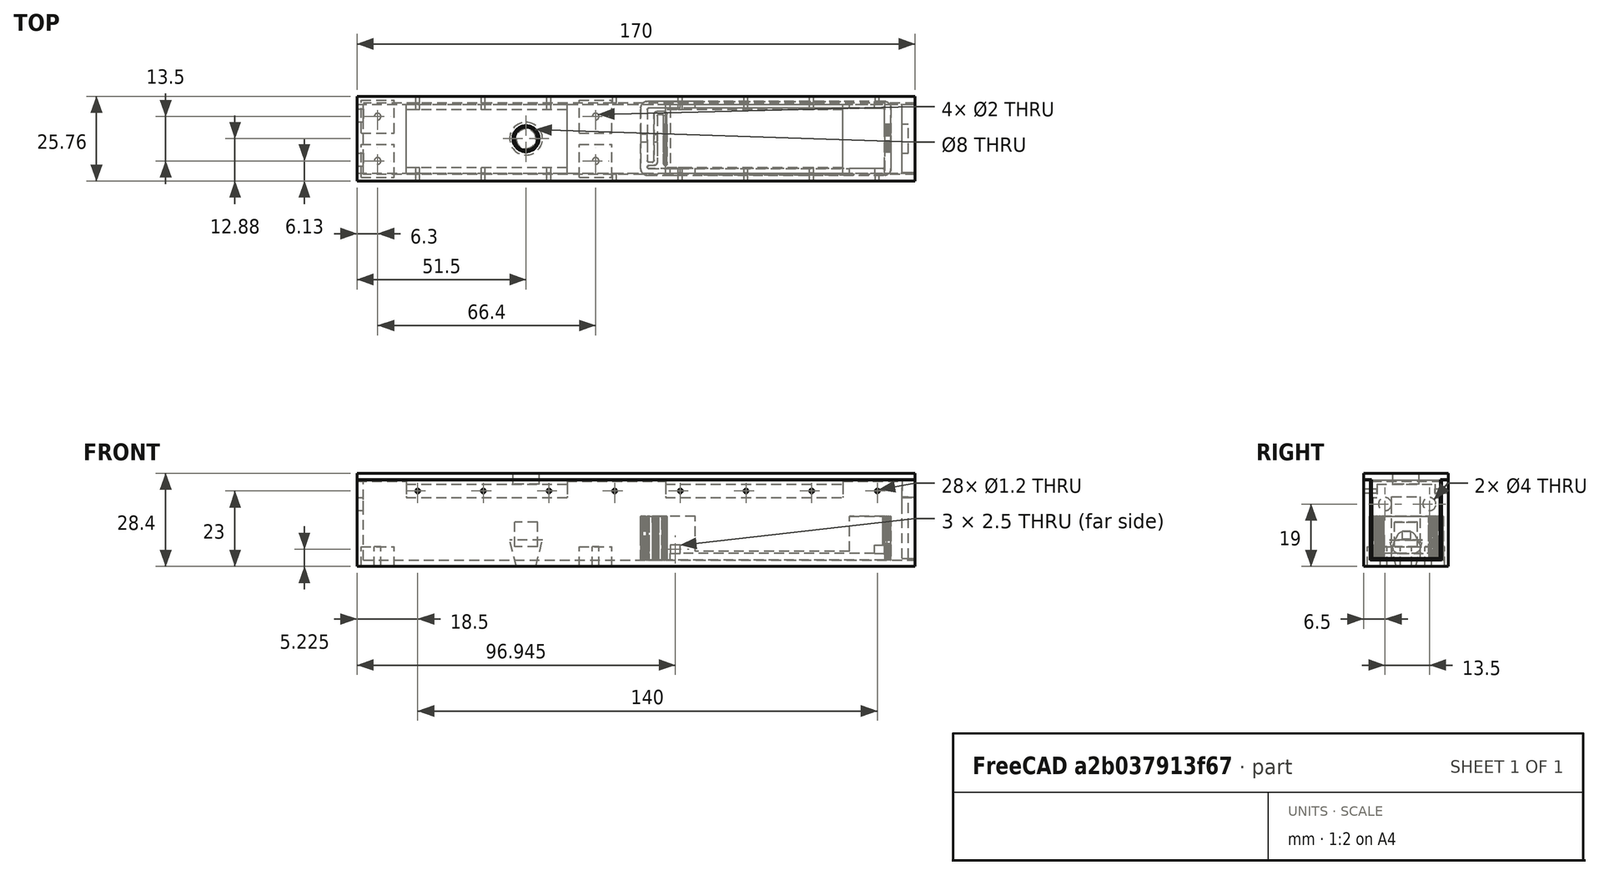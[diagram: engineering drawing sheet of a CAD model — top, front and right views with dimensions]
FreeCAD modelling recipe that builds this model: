
FCSTD DOCUMENT  (FreeCAD 0.19R)
Label: hv-1_box
License: All rights reserved
LicenseURL: http://en.wikipedia.org/wiki/All_rights_reserved
objects: Part::Box×14, Part::Cylinder×5, Part::Cut×5, Part::FeaturePython×4, Part::Feature×4, Part::MultiFuse×3, App::Part×3, Part::Compound×2, Spreadsheet::Sheet×1, Part::Cone×1
note: 38 computed .brp shape members not serialized (recipe doc carries the construction recipe); baked Part::Feature solids carry a one-line shape summary decoded from their .brp

FEATURE [Part::Box] Box  label="Cube"
  AttacherType = Attacher::AttachEngine3D
  Height = 26.3
  Length = 170
  Width = 25.76
  expr: Length = <<p>>.box_sz_x
  expr: Width = <<p>>.box_sz_y
  expr: Height = <<p>>.box_sz_z
FEATURE [Spreadsheet::Sheet] Spreadsheet  label="p"
  cells = A1=pcb_sz_x; B1(pcb_sz_x)=71; A2=pcb_sz_y; B2(pcb_sz_y)=17.76; A3=pcb_sz_z; B3(pcb_sz_z)=1.3; A4=hole_dist_x; B4(hole_dist_x)=66.40000000000001; A5=hole_dist_y; B5(hole_dist_y)=13.5; A6=pcb_under; B6(pcb_under)=4; A7=pcb_above; B7(pcb_above)=11; A8=wall; B8(wall)=2; A9=hole_d; B9(hole_d)=2; A10=box_sz_y; B10(box_sz_y)==pcb_sz_y + 2 * wall + 4; A11=box_sz_x; B11(box_sz_x)==pcb_sz_x + 2 * wall + 95; A12=box_sz_z; B12(box_sz_z)==pcb_under + pcb_sz_z + pcb_above + wall + 8
FEATURE [Part::Cylinder] Cylinder
  Angle = 360
  AttacherType = Attacher::AttachEngine3D
  Height = 14
  Radius = 1
  expr: Radius = <<p>>.hole_d / 2
  expr: Height = <<p>>.pcb_under + 10
FEATURE [Part::Box] Box001  label="Cube001"
  AttacherType = Attacher::AttachEngine3D
  Height = 26.3
  Length = 170
  Placement = pos=(2,2,2) rot=(0,0,1;0rad)
  Width = 21.76
  expr: Length = <<p>>.box_sz_x
  expr: Width = <<p>>.box_sz_y - 2 * <<p>>.wall
  expr: Height = <<p>>.box_sz_z
  expr: .Placement.Base.z = <<p>>.wall
  expr: .Placement.Base.x = <<p>>.wall
  expr: .Placement.Base.y = <<p>>.wall
FEATURE [Part::Cylinder] Cylinder002
  Angle = 360
  AttacherType = Attacher::AttachEngine3D
  Height = 100
  Placement = pos=(18.5,-32.5,23) rot=(-1,0,0;1.5708rad)
  Radius = 0.6
FEATURE [Part::FeaturePython] Array002  # Draft array (typed FeaturePython)
  Angle = 360
  ArrayType = 0
  Axis = (0,0,1)
  Base = -> Cylinder002
  Center = (0,0,0)
  Fuse = false
  IntervalAxis = (0,0,0)
  IntervalX = (20,0,0)
  IntervalY = (0,1,0)
  IntervalZ = (0,0,1)
  NumberPolar = 1
  NumberX = 8
  NumberY = 1
  NumberZ = 1
FEATURE [Part::Box] Box003  label="Cube003"
  AttacherType = Attacher::AttachEngine3D
  Height = 6
  Length = 10
  Placement = pos=(-5,-5,0) rot=(0,0,1;0rad)
  Width = 10
  expr: Height = <<p>>.pcb_under + <<p>>.wall
FEATURE [Part::Cut] Cut
  Base = -> Box003
  Tool = -> Cylinder
FEATURE [Part::FeaturePython] Array  # Draft array (typed FeaturePython)
  Angle = 360
  ArrayType = 0
  Axis = (0,0,1)
  Base = -> Cut
  Center = (0,0,0)
  Fuse = false
  IntervalAxis = (0,0,0)
  IntervalX = (66.4,0,0)
  IntervalY = (0,13.5,0)
  IntervalZ = (0,0,1)
  NumberPolar = 1
  NumberX = 2
  NumberY = 2
  NumberZ = 1
  Placement = pos=(6.3,6.13,0) rot=(0,0,1;0rad)
  expr: .IntervalX.x = <<p>>.hole_dist_x
  expr: .IntervalY.y = <<p>>.hole_dist_y
  expr: .Placement.Base.y = (<<p>>.pcb_sz_y + 2 * <<p>>.wall - <<p>>.hole_dist_y) / 2 + 2
  expr: .Placement.Base.x = (<<p>>.pcb_sz_x + 2 * <<p>>.wall - <<p>>.hole_dist_x) / 2 + 2
FEATURE [Part::Cylinder] Cylinder003
  Angle = 360
  AttacherType = Attacher::AttachEngine3D
  Height = 10
  Placement = pos=(-4,6.5,19) rot=(0,1,0;1.5708rad)
  Radius = 2
FEATURE [Part::FeaturePython] Array001  # Draft array (typed FeaturePython)
  Angle = 360
  ArrayType = 0
  Axis = (0,0,1)
  Base = -> Cylinder003
  Center = (0,0,0)
  Fuse = false
  IntervalAxis = (0,0,0)
  IntervalX = (1,0,0)
  IntervalY = (0,13.5,0)
  IntervalZ = (0,0,1)
  NumberPolar = 1
  NumberX = 1
  NumberY = 2
  NumberZ = 1
  expr: .IntervalY.y = <<p>>.hole_dist_y
FEATURE [Part::MultiFuse] Fusion
  Shapes = -> [Box001,Array001,Array002]
FEATURE [Part::Cut] Cut001
  Base = -> Box
  Tool = -> Fusion
FEATURE [App::Part] Part001  label="lid part"
  Origin = -> Origin001
FEATURE [Part::Box] Box004  label="Cube004"
  AttacherType = Attacher::AttachEngine3D
  Height = 6
  Length = 170
  Placement = pos=(0,2.4,21) rot=(0,0,1;0rad)
  Width = 20.96
  expr: Width = <<p>>.box_sz_y - 2 * <<p>>.wall - 0.8
  expr: Length = <<p>>.box_sz_x
  expr: .Placement.Base.y = <<p>>.wall + 0.4
FEATURE [Part::Box] Box005  label="Cube005"
  AttacherType = Attacher::AttachEngine3D
  Height = 6
  Length = 166
  Placement = pos=(0,4,19) rot=(0,0,1;0rad)
  Width = 17.76
  expr: Width = <<p>>.box_sz_y - 4 * <<p>>.wall
  expr: Length = <<p>>.box_sz_x - 2 * <<p>>.wall
  expr: .Placement.Base.y = 2 * <<p>>.wall
FEATURE [Part::Box] Box006  label="Cube006"
  AttacherType = Attacher::AttachEngine3D
  Height = 2
  Length = 170
  Placement = pos=(0,0,26.4) rot=(0,0,1;0rad)
  Width = 25.76
  expr: Width = <<p>>.box_sz_y
  expr: Length = <<p>>.box_sz_x
  expr: Height = <<p>>.wall
FEATURE [Part::FeaturePython] Array003  # Draft array (typed FeaturePython)
  Angle = 360
  ArrayType = 0
  Axis = (0,0,1)
  Base = -> Cylinder002
  Center = (0,0,0)
  Fuse = false
  IntervalAxis = (0,0,0)
  IntervalX = (20,0,0)
  IntervalY = (0,1,0)
  IntervalZ = (0,0,1)
  NumberPolar = 1
  NumberX = 8
  NumberY = 1
  NumberZ = 1
FEATURE [Part::Box] Box009  label="Cube009"
  AttacherType = Attacher::AttachEngine3D
  Height = 10
  Length = 15
  Placement = pos=(0,0,16) rot=(0,0,1;0rad)
  Width = 25.76
  expr: Width = <<p>>.box_sz_y
FEATURE [Part::Box] Box010  label="Cube010"
  AttacherType = Attacher::AttachEngine3D
  Height = 10
  Length = 30
  Placement = pos=(64,0,16) rot=(0,0,1;0rad)
  Width = 25.76
  expr: Width = <<p>>.box_sz_y
FEATURE [Part::Box] Box011  label="Cube011"
  AttacherType = Attacher::AttachEngine3D
  Height = 10
  Length = 18
  Placement = pos=(148,0,16) rot=(0,0,1;0rad)
  Width = 25.76
  expr: Width = <<p>>.box_sz_y
FEATURE [Part::Cylinder] Cylinder004
  Angle = 360
  AttacherType = Attacher::AttachEngine3D
  Height = 10
  Placement = pos=(51.5,12.88,20) rot=(0,0,1;0rad)
  Radius = 4
  expr: .Placement.Base.y = <<p>>.box_sz_y / 2
FEATURE [Part::Box] Box008  label="Cube008"
  AttacherType = Attacher::AttachEngine3D
  Height = 25.8
  Length = 2
  Placement = pos=(168,2.5,2.5) rot=(0,0,1;0rad)
  Width = 20.76
  expr: Width = <<p>>.box_sz_y - 2 * <<p>>.wall - 1
  expr: .Placement.Base.x = <<p>>.box_sz_x - <<p>>.wall
  expr: .Placement.Base.y = <<p>>.wall + 0.5
  expr: Height = <<p>>.box_sz_z - 0.5
  expr: .Placement.Base.z = <<p>>.wall + 0.5
  expr: Length = <<p>>.wall
FEATURE [Part::Box] Box007  label="Cube007"
  AttacherType = Attacher::AttachEngine3D
  Height = 22.2
  Length = 2
  Placement = pos=(166,2.5,2.5) rot=(0,0,1;0rad)
  Width = 20.76
  expr: .Placement.Base.x = <<p>>.box_sz_x - 2 * <<p>>.wall
  expr: .Placement.Base.y = <<p>>.wall + 0.5
  expr: Height = <<p>>.box_sz_z - 2 * <<p>>.wall - 0.1
  expr: .Placement.Base.z = <<p>>.wall + 0.5
  expr: Length = <<p>>.wall
  expr: Width = <<p>>.box_sz_y - 2 * <<p>>.wall - 1
FEATURE [Part::MultiFuse] Fusion001
  Shapes = -> [Box004,Box006,Box008,Box007]
FEATURE [Part::Box] Box012  label="Cube012"
  AttacherType = Attacher::AttachEngine3D
  Height = 21.3
  Length = 2
  Placement = pos=(166,8.5,0) rot=(0,0,1;0rad)
  Width = 8.76
  expr: .Placement.Base.x = <<p>>.box_sz_x - 2 * <<p>>.wall
  expr: .Placement.Base.y = <<p>>.wall + 6.5
  expr: Height = <<p>>.box_sz_z - <<p>>.wall - 3
  expr: .Placement.Base.z = 0
  expr: Length = <<p>>.wall
  expr: Width = <<p>>.box_sz_y - 2 * <<p>>.wall - 13
FEATURE [Part::MultiFuse] Fusion002  label="cut out fusion"
  Shapes = -> [Box005,Array003,Box009,Box010,Box011,Cylinder004,Box012]
FEATURE [Part::Cut] Cut002  label="lid cut"
  Base = -> Fusion001
  Tool = -> Fusion002
FEATURE [Part::Cylinder] Cylinder005
  Angle = 360
  AttacherType = Attacher::AttachEngine3D
  Height = 7.5
  Placement = pos=(51.5,12.9,6) rot=(0,0,1;0rad)
  Radius = 3.5
FEATURE [Part::Cone] Cone
  Angle = 360
  AttacherType = Attacher::AttachEngine3D
  Height = 8
  Placement = pos=(51.5,12.9,0) rot=(0,0,1;0rad)
  Radius1 = 3
  Radius2 = 5
FEATURE [Part::Compound] Compound
  Links = -> [Cylinder005,Cone]
FEATURE [App::Part] Part002  label="button part"
  Group = -> [Cylinder005,Cone,Compound]
  Origin = -> Origin002
FEATURE [Part::Box] Box013  label="Cube013"
  AttacherType = Attacher::AttachEngine3D
  Height = 10
  Length = 100
  Placement = pos=(74,0,19) rot=(0,0,1;0rad)
  Width = 30
FEATURE [Part::Feature] single_cell_charger001001  label="single_cell_charger002"
  shape: bbox 84 x 22 x 23.09 mm, 5913 faces, 0 solids (baked)
FEATURE [Part::Cut] Cut003
  Base = -> single_cell_charger001001
  Tool = -> Box013
FEATURE [Part::Feature] Mesh001  label="battery_box"
  shape: bbox 84 x 22 x 18.6 mm, 12105 faces, 0 solids (baked)
FEATURE [Part::Feature] _8650_X1001001001
  Placement = pos=(121,13,-30) rot=(0,0,1;1.5708rad)
  shape: bbox 76.2 x 22.5 x 15.45 mm, 1948 faces, 0 solids (baked)
FEATURE [Part::Box] Box014  label="battery flex box extraction cube"
  AttacherType = Attacher::AttachEngine3D
  Height = 20
  Length = 47
  Placement = pos=(103,0,3) rot=(0,0,1;0rad)
  Width = 38
FEATURE [Part::Feature] _8650_X1001001001_solid  label="_8650_X1001001001 (Solid)"
  shape: bbox 76.2 x 22.5 x 15.45 mm, 1948 faces (baked)
FEATURE [Part::Cut] Cut004  label="battery flex box cut"
  Base = -> _8650_X1001001001_solid
  Placement = pos=(0,0,1.6) rot=(0,0,1;0rad)
  Tool = -> Box014
FEATURE [Part::Compound] Compound001  label="bottom compound"
  Links = -> [Array,Cut001,Cut004]
FEATURE [App::Part] Part  label="box part"
  Group = -> [Box005,Cylinder002,Box003,Array,Array001,Array003,Array002,Box008,Cylinder003,Cylinder,Cylinder004,Box004,Fusion,Box010,Box012,Box001,Cut,Box007,Cut002,Fusion001,Box006,Fusion002,Box009,Cut001,Box011,Box,Compound001]
  Origin = -> Origin
